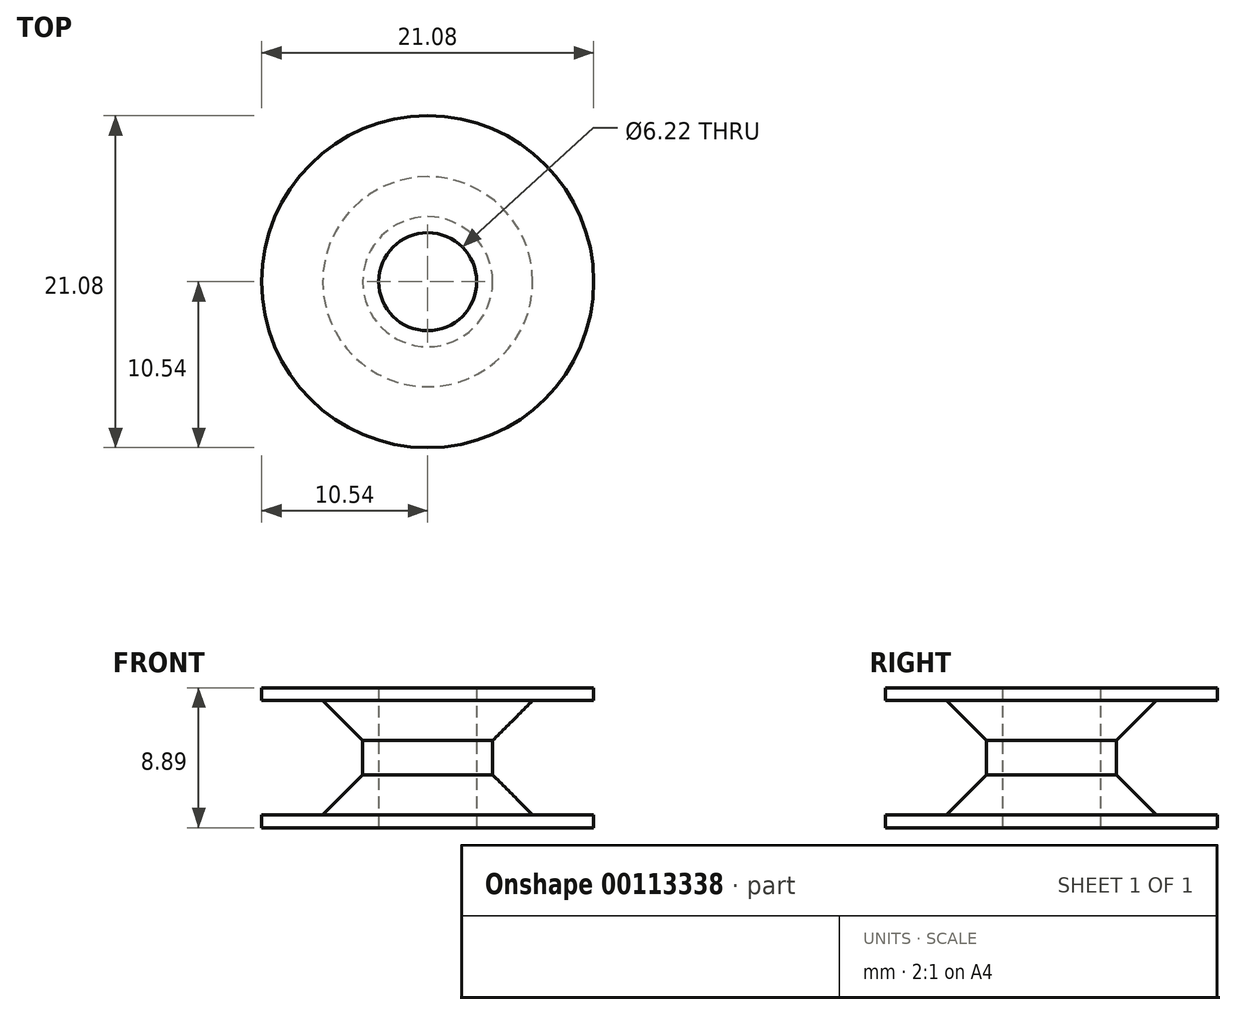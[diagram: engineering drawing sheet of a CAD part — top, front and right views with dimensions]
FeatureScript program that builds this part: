
annotation { "Feature Type Name" : "Feature", "Feature Type Description" : "" }
export const myFeature = defineFeature(function(context is Context, id is Id, definition is map)
    precondition{}
    {
        {
            var Q0;
            Q0=qCreatedBy(makeId("Top.planeOp"),FACE);
            var sketch = newSketch(context, id + "F0", { "sketchPlane" : qUnion([Q0])});
            skCircle(sketch, "E0", {"center": v(0, 0) * mm, "radius": 10.54 * mm});
            skSolve(sketch);
        }
        {
            var Q0;
            Q0 = qSketchRegion(id + "F0", true);
            extrude(context, id + "F1", {"entities" : qUnion([Q0]), "depth" : 0.81 * mm});
        }
        {
            var Q0;
            Q0=qCreatedBy(makeId("Top.planeOp"),FACE);
            var sketch = newSketch(context, id + "F2", { "sketchPlane" : qUnion([Q0])});
            skCircle(sketch, "E1", {"center": v(0, 0) * mm, "radius": 4.13 * mm});
            skSolve(sketch);
        }
        {
            var Q0;
            Q0 = qSketchRegion(id + "F2", true);
            extrude(context, id + "F3", {"entities" : qUnion([Q0]), "operationType" : NewBodyOperationType.ADD, "depth" : 8.9 * mm});
        }
        {
            var Q0;
            Q0=makeQuery(id+"F3.opExtrude","CAP_FACE",FACE,{"disambiguationData":[OSD([sQuery(id+"F2.wireOp",EDGE,"E1")])],"isStart":false});
            cPlane(context, id + "F4", {"entities" : qUnion([Q0]), "cplaneType" : CPlaneType.OFFSET, "offset" : 0 * mm, "width" : 152.4 * mm, "height" : 152.4 * mm});
        }
        {
            var Q0;
            Q0=qCreatedBy(id+"F4.planeOp",FACE);
            var sketch = newSketch(context, id + "F5", { "sketchPlane" : qUnion([Q0])});
            skCircle(sketch, "E2", {"center": v(0, 0) * mm, "radius": 10.54 * mm});
            skSolve(sketch);
        }
        {
            var Q0;
            Q0 = qSketchRegion(id + "F5", true);
            extrude(context, id + "F6", {"entities" : qUnion([Q0]), "operationType" : NewBodyOperationType.ADD, "oppositeDirection" : true, "depth" : 0.81 * mm});
        }
        {
            var Q0;
            Q0=qCreatedBy(makeId("Top.planeOp"),FACE);
            var sketch = newSketch(context, id + "F7", { "sketchPlane" : qUnion([Q0])});
            skCircle(sketch, "E3", {"center": v(0, 0) * mm, "radius": 3.11 * mm});
            skSolve(sketch);
        }
        {
            var Q0;
            Q0 = qSketchRegion(id + "F7", true);
            extrude(context, id + "F8", {"entities" : qUnion([Q0]), "operationType" : NewBodyOperationType.REMOVE, "depth" : 8.9 * mm});
        }
        {
            var Q0;
            Q0=makeQuery(id+"F6.boolean.opBoolean","INTERSECT",EDGE,{"derivedFrom":[makeQuery(id+"F3.opExtrude","SWEPT_FACE",FACE,{"disambiguationData":[OSD([sQuery(id+"F2.wireOp",EDGE,"E1")])]}),makeQuery(id+"F6.opExtrude","CAP_FACE",FACE,{"disambiguationData":[OSD([sQuery(id+"F5.wireOp",EDGE,"E2")])],"isStart":false})]});
            var Q1;
            Q1=makeQuery(id+"F3.boolean.opBoolean","INTERSECT",EDGE,{"derivedFrom":[makeQuery(id+"F1.opExtrude","CAP_FACE",FACE,{"disambiguationData":[OSD([sQuery(id+"F0.wireOp",EDGE,"E0")])],"isStart":false}),makeQuery(id+"F3.opExtrude","SWEPT_FACE",FACE,{"disambiguationData":[OSD([sQuery(id+"F2.wireOp",EDGE,"E1")])]})]});
            chamfer(context, id + "F9", {"entities" : qUnion([Q0, Q1]), "width" : 2.54 * mm, "tangentPropagation" : true});
        }
    });
